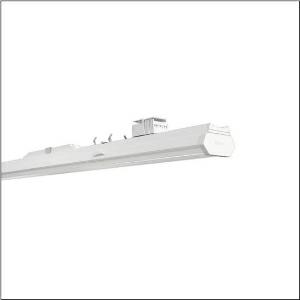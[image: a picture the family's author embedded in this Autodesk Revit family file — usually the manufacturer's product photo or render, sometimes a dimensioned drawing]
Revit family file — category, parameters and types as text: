
# Revit family: licross_r__11_protected_mo_51tp127n58xf_03c6
name_source: partatom
category: Lighting Fixtures
units: mm (PartAtom-declared; Revit-internal decimal feet)

## family parameters
Cut with Voids When Loaded = No
Host = Face
Light Source = No
Part Type = Normal
Room Calculation Point = No
Round Connector Dimension = Use Diameter
Shared = No

## types (1)
- Licross® 11 Protected MO (1 x LED, 8120 lm, 47.6 W, 5000K)
    Apparent Load = 48 VA
    CIE Flux Codes = 73 92 98 99 100
    Color Rendering = 80
    Color Temperature = 5000K
    Default Elevation = 1800 mm
    Description = Licross® 11 Protected MOluminaire insert, length: 1.500mm, width: 90mm, height: 101mm, LED rated luminous flux: 8.120lm, light colour: 850, control gear: ON/OFF, control gear: ECG, with plug, 3-pole, with phase selection, mains connection: 220..240V, AC, 50/60Hz, halogen-free wiring, primary optical cover: cover, of PMMA, light emission: direct with ceiling illumination distribution, protection rating (complete): IP64, insulation class (complete): insulation class I (protective earthing), certification: CE, ENEC, VDE, protection symbol: D if used in an environment with conductive dust loads with corresponding accessories, permissible ambient temperature for indoor applications: -35..+45°C, reducing of maximum allowable ambient temperature of 5°C with ceiling mounting, corresponds to IFS (International Featured Standards) requirements for safety and quality in the food industry, packaging unit: 1 piece
    Height = 92 mm
    Lamp = 1 x LED
    Lamp Light Flux = 8120 lm
    Lamp Power = 47.6 W
    Lamp count = 1
    Length = 1500 mm
    Luminous efficacy = 171 lm/W
    Manufacturer = Siteco
    ModVariant = No
    Model = 51TP127N58XF
    Mounting Place = Ceiling
    Mounting Type = Pendant
    Number of Poles = 1
    OnlyDefault = Yes
    Power Factor = 1
    Product Name = Licross® 11 Protected MO
    Product group = luminaire insert
    ProductGroupID = 902
    Protection Class = Protection class I
    Protection Degree = IP 64
    RLX_Detail_Level = 1
    RlxData = <blob elided: 20445 chars, md5=559ea3a1>
    Socket = socket
    Standby Power = 0 W
    System Light Flux = 8120 lm
    System Power = 48 W
    Type Comments = Product without accessories
    Type Image = l_1256148.jpg
    URL = http://relux.com
    VarID = ---
    Voltage = 0 V
    Weight = 0.00 kg
    Width = 88 mm

## geometry (parser evidence)
native form markers: Blend x4, Sweep x11
no freeform markers — native parametric forms only
